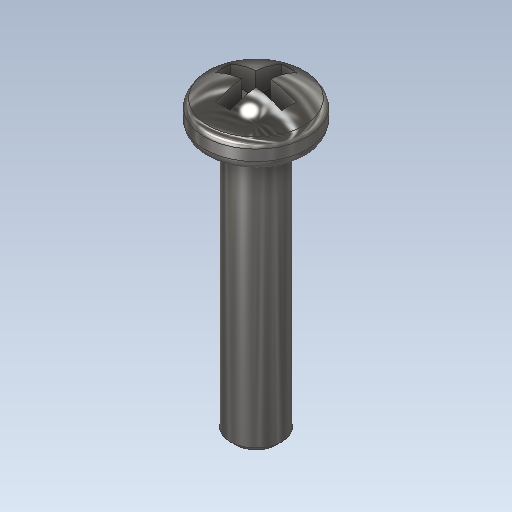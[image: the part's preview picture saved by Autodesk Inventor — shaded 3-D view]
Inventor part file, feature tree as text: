
AUTODESK INVENTOR PART (.ipt)
format: ipt  version: 2020.1 (Build 241239000, 239)  size: 244,736 bytes
history: native  units: mm
features: chamfer x2, sketch x2, revolve x1, fillet x1, plane x1, extrude x1, other x1
ambient origin geometry x8: Origin, YZ Plane, XZ Plane, XY Plane, X Axis, Y Axis, Z Axis, Center Point
bodies: Solid1 (feature_tree)
feature tree (9):
  revolve  "Revolution1"  [1 undecoded]
  chamfer  "Chamfer1"  Distance=2.5mm
  fillet  "Fillet1"  Radius=2.5mm
  plane  "Work Plane1"
  extrude  "Extrusion1"  Depth=2.5mm
  chamfer  "Chamfer2"  Angle=90.0deg  [1 undecoded]
  sketch  "Sketch1"  dims[d0=25.4mm d1=2.5mm]
  other  "Image1"
  sketch  "Sketch4"  dims[d2=4.5mm d4=2.5mm d31=2.5mm d33=2.5mm d34=90.0deg d35=0.5mm d36=2.0mm d37=45.0deg d38=1.0mm d41=0.0mm d57=2.5mm d58=1.4mm d59=2.5mm d60=1.4mm d61=2.5mm d62=2.5mm d63=1.4mm d64=90.0deg d65=2.5mm d66=1.4mm d67=90.0deg d68=3.0mm d69=0.0mm d70=0.69999mm d71=2.0mm d72=45.0deg]
note: 2 required parameter values undecoded (feature->parameter linkage not recoverable at this tier; creation-order binding heuristic only, values carry confidence <= 0.55)